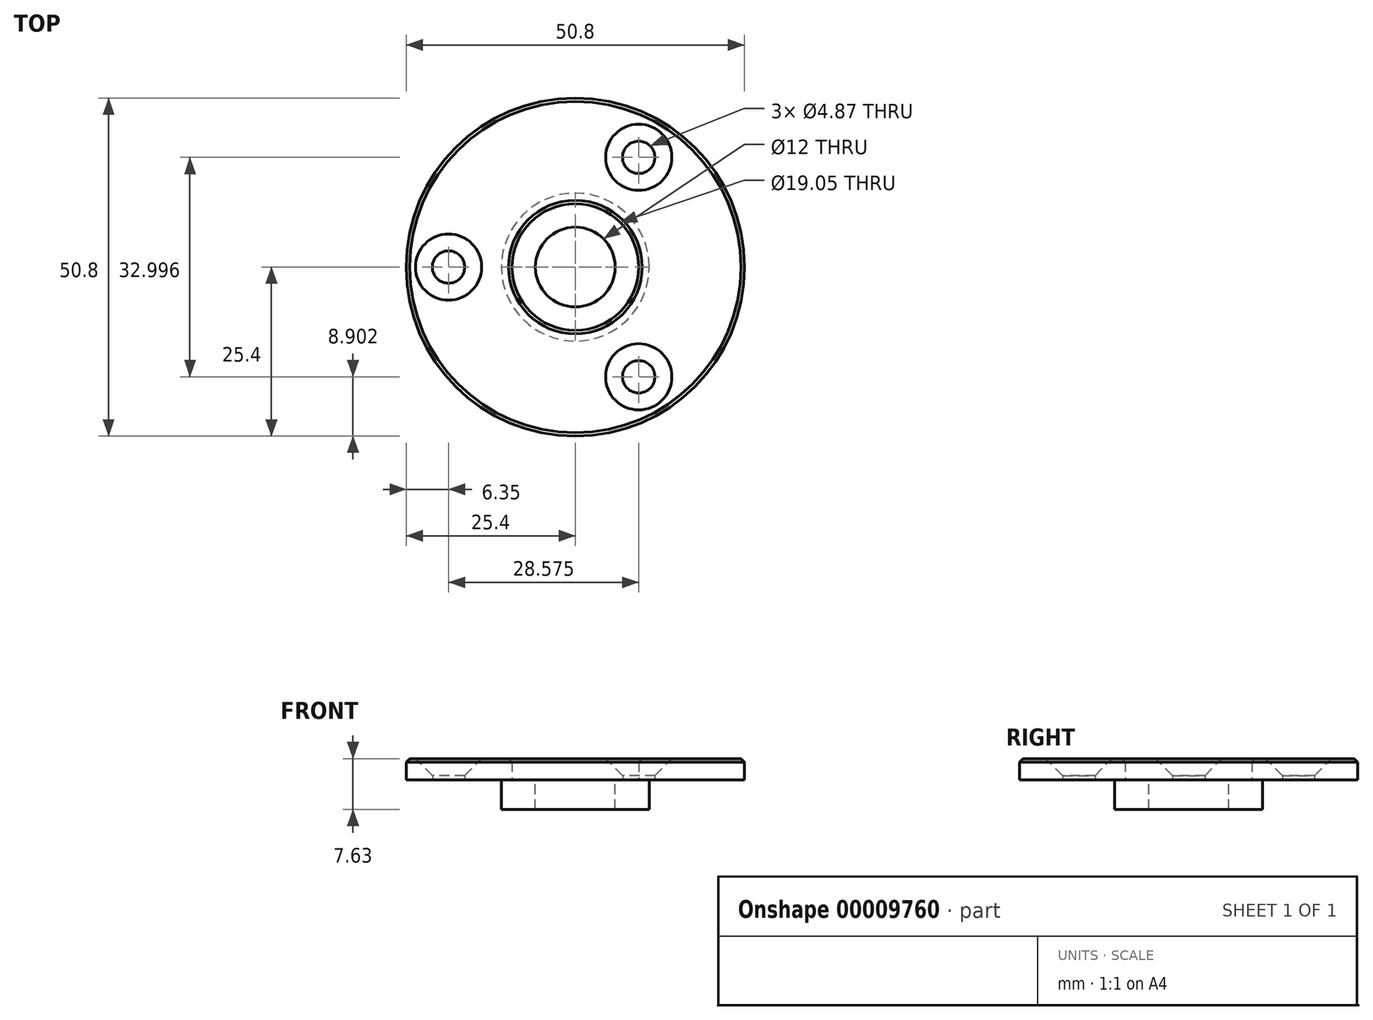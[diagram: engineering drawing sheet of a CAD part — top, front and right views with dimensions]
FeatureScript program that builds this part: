
annotation { "Feature Type Name" : "Feature", "Feature Type Description" : "" }
export const myFeature = defineFeature(function(context is Context, id is Id, definition is map)
    precondition{}
    {
        {
            var Q0;
            Q0=qCreatedBy(makeId("Top.planeOp"),FACE);
            var sketch = newSketch(context, id + "F0", { "sketchPlane" : qUnion([Q0])});
            skCircle(sketch, "E0", {"center": v(0, 0) * mm, "radius": 25.4 * mm});
            skCircle(sketch, "E1", {"center": v(0, 0) * mm, "radius": 9.53 * mm});
            skCircle(sketch, "E2", {"center": v(0, 0) * mm, "radius": 6 * mm});
            skCircle(sketch, "E3", {"center": v(0, 0) * mm, "radius": 19.05 * mm, "construction": true});
            skCircle(sketch, "E4", {"center": v(-19.05, 0) * mm, "radius": 4.57 * mm});
            skCircle(sketch, "E5", {"center": v(-19.05, 0) * mm, "radius": 2.43 * mm});
            skCircle(sketch, "E6.1.0", {"center": v(9.52, -16.5) * mm, "radius": 4.57 * mm});
            skCircle(sketch, "E6.1.1", {"center": v(9.52, -16.5) * mm, "radius": 2.43 * mm});
            skCircle(sketch, "E6.2.0", {"center": v(9.52, 16.5) * mm, "radius": 4.57 * mm});
            skCircle(sketch, "E6.2.1", {"center": v(9.52, 16.5) * mm, "radius": 2.43 * mm});
            skCircle(sketch, "E7", {"center": v(0, 0) * mm, "radius": 11.11 * mm});
            skSolve(sketch);
        }
        {
            var Q0;
            Q0=makeQuery(id+"F0.imprint","IMPRINT",FACE,{"disambiguationData":[TD([[makeQuery(id+"F0.imprint","IMPRINT",EDGE,{"derivedFrom":sQuery(id+"F0.wireOp",EDGE,"E0")}),1.0]])]});
            var Q1;
            Q1=makeQuery(id+"F0.imprint","IMPRINT",FACE,{"disambiguationData":[TD([[makeQuery(id+"F0.imprint","IMPRINT",EDGE,{"derivedFrom":sQuery(id+"F0.wireOp",EDGE,"E6.2.0")}),1.0]])]});
            var Q2;
            Q2=makeQuery(id+"F0.imprint","IMPRINT",FACE,{"disambiguationData":[TD([[makeQuery(id+"F0.imprint","IMPRINT",EDGE,{"derivedFrom":sQuery(id+"F0.wireOp",EDGE,"E4")}),1.0]])]});
            var Q3;
            Q3=makeQuery(id+"F0.imprint","IMPRINT",FACE,{"disambiguationData":[TD([[makeQuery(id+"F0.imprint","IMPRINT",EDGE,{"derivedFrom":sQuery(id+"F0.wireOp",EDGE,"E6.1.0")}),1.0]])]});
            var Q4;
            Q4=makeQuery(id+"F0.imprint","IMPRINT",FACE,{"disambiguationData":[TD([[makeQuery(id+"F0.imprint","IMPRINT",EDGE,{"derivedFrom":sQuery(id+"F0.wireOp",EDGE,"E1")}),-1.0]])]});
            extrude(context, id + "F1", {"entities" : qUnion([Q0, Q1, Q2, Q3, Q4]), "depth" : 3.17 * mm});
        }
        {
            var Q0;
            Q0=makeQuery(id+"F0.imprint","IMPRINT",FACE,{"disambiguationData":[TD([[makeQuery(id+"F0.imprint","IMPRINT",EDGE,{"derivedFrom":sQuery(id+"F0.wireOp",EDGE,"E0")}),1.0]])]});
            var sketch = newSketch(context, id + "F2", { "sketchPlane" : qUnion([Q0])});
            skCircle(sketch, "E8.0", {"center": v(0, 0) * mm, "radius": 6 * mm});
            skCircle(sketch, "E9.0", {"center": v(0, 0) * mm, "radius": 9.53 * mm});
            skCircle(sketch, "E10.0", {"center": v(0, 0) * mm, "radius": 11.11 * mm});
            skSolve(sketch);
        }
        {
            var Q0;
            Q0=makeQuery(id+"F0.imprint","IMPRINT",FACE,{"disambiguationData":[TD([[makeQuery(id+"F0.imprint","IMPRINT",EDGE,{"derivedFrom":sQuery(id+"F0.wireOp",EDGE,"E1")}),-1.0]])]});
            var Q1;
            Q1=makeQuery(id+"F0.imprint","IMPRINT",FACE,{"disambiguationData":[TD([[makeQuery(id+"F0.imprint","IMPRINT",EDGE,{"derivedFrom":sQuery(id+"F0.wireOp",EDGE,"E1")}),1.0]])]});
            extrude(context, id + "F3", {"entities" : qUnion([Q0, Q1]), "oppositeDirection" : true, "depth" : 4.44 * mm});
        }
        {
            var Q0;
            Q0=makeQuery(id+"F1.opExtrude","CAP_EDGE",EDGE,{"disambiguationData":[OSD([sQuery(id+"F0.wireOp",EDGE,"E6.1.1")])],"isStart":false});
            var Q1;
            Q1=makeQuery(id+"F1.opExtrude","CAP_EDGE",EDGE,{"disambiguationData":[OSD([sQuery(id+"F0.wireOp",EDGE,"E5")])],"isStart":false});
            var Q2;
            Q2=makeQuery(id+"F1.opExtrude","CAP_EDGE",EDGE,{"disambiguationData":[OSD([sQuery(id+"F0.wireOp",EDGE,"E6.2.1")])],"isStart":false});
            chamfer(context, id + "F4", {"entities" : qUnion([Q0, Q1, Q2]), "width" : 2.54 * mm, "tangentPropagation" : true});
        }
        {
            var Q0;
            Q0=makeQuery(id+"F1.opExtrude","CAP_EDGE",EDGE,{"disambiguationData":[OSD([sQuery(id+"F0.wireOp",EDGE,"E0")])],"isStart":false});
            chamfer(context, id + "F5", {"entities" : qUnion([Q0]), "width" : 0.5 * mm, "tangentPropagation" : true});
        }
        {
            var Q0;
            Q0=makeQuery(id+"F1.opExtrude","CAP_EDGE",EDGE,{"disambiguationData":[OSD([sQuery(id+"F0.wireOp",EDGE,"E1")])],"isStart":false});
            chamfer(context, id + "F6", {"entities" : qUnion([Q0]), "width" : 0.5 * mm, "tangentPropagation" : true});
        }
    });
